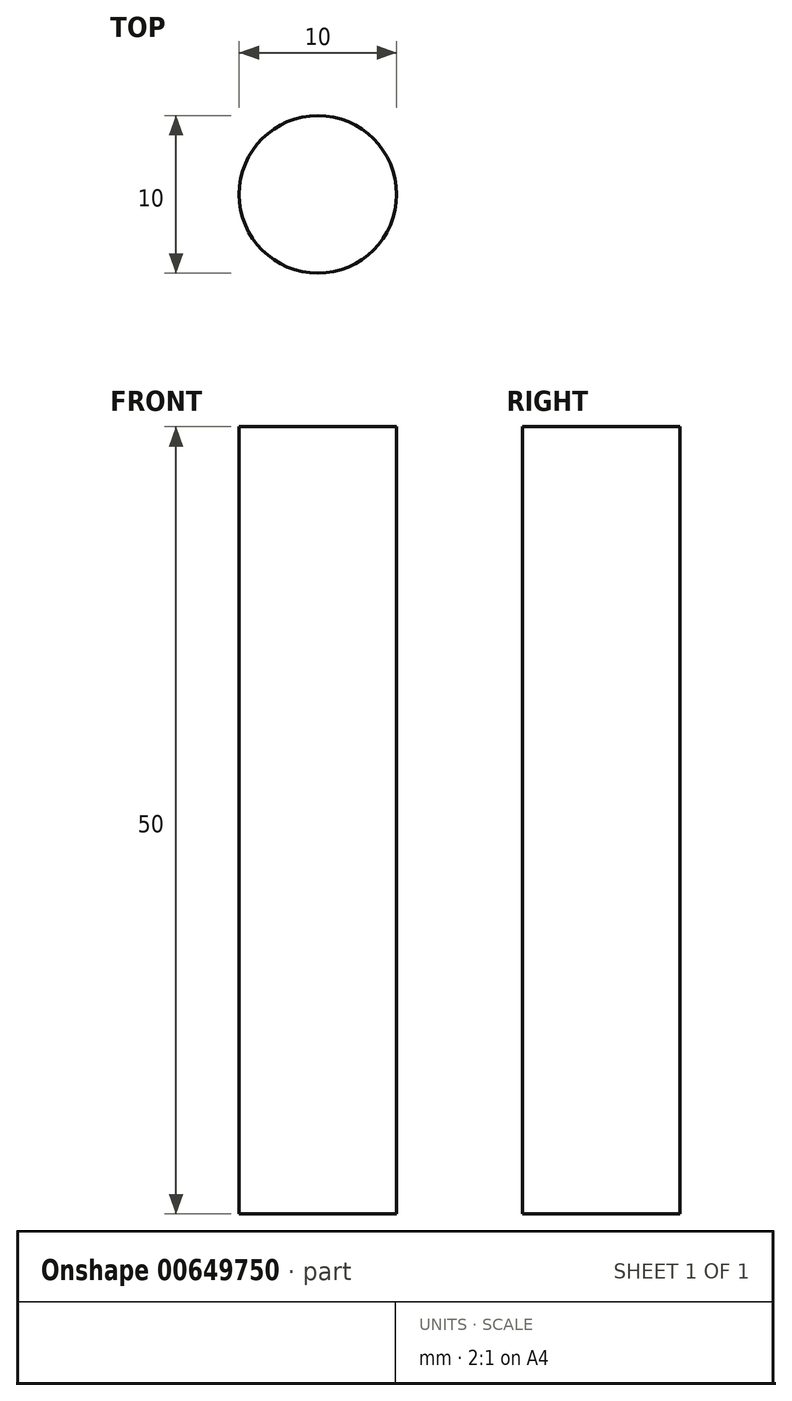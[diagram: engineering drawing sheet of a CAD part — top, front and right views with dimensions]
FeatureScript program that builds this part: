
annotation { "Feature Type Name" : "Feature", "Feature Type Description" : "" }
export const myFeature = defineFeature(function(context is Context, id is Id, definition is map)
    precondition{}
    {
        {
            var Q0;
            Q0=qCreatedBy(makeId("Top.planeOp"),FACE);
            var sketch = newSketch(context, id + "F0", { "sketchPlane" : qUnion([Q0])});
            skCircle(sketch, "E0", {"center": v(0, 0) * mm, "radius": 5 * mm});
            skSolve(sketch);
        }
        {
            var Q0;
            Q0=makeQuery(id+"F0.imprint","IMPRINT",FACE,{"disambiguationData":[TD([[makeQuery(id+"F0.imprint","IMPRINT",EDGE,{"derivedFrom":sQuery(id+"F0.wireOp",EDGE,"E0")}),1.0]])]});
            extrude(context, id + "F1", {"entities" : qUnion([Q0]), "depth" : 50 * mm, "offsetDistance" : 25 * mm});
        }
    });
